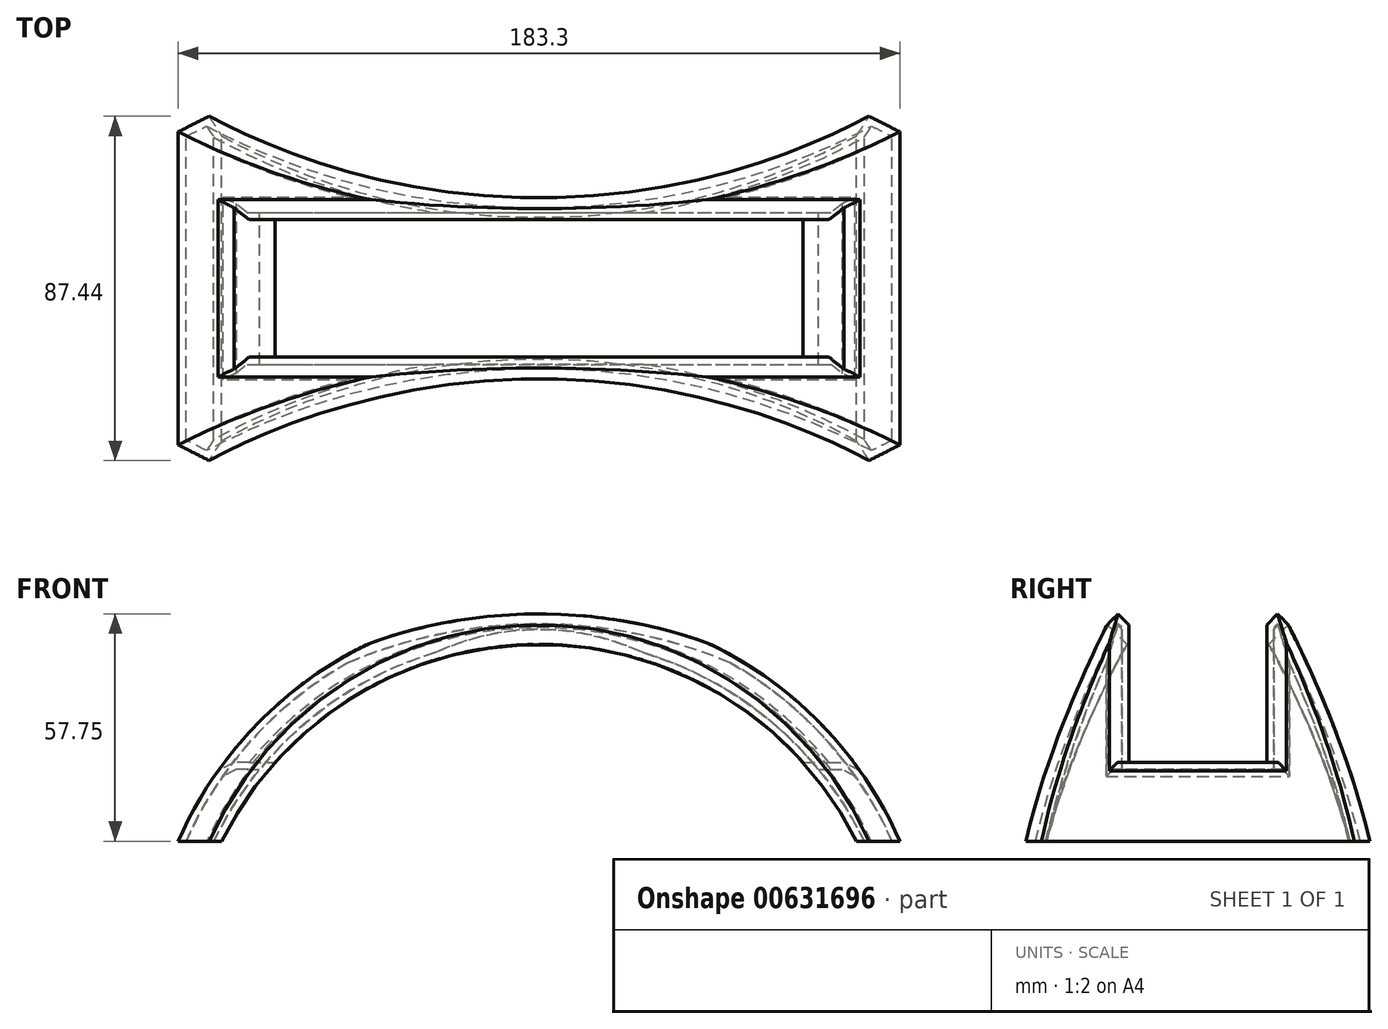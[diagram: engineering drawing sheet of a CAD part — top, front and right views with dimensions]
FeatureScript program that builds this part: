
annotation { "Feature Type Name" : "Feature", "Feature Type Description" : "" }
export const myFeature = defineFeature(function(context is Context, id is Id, definition is map)
    precondition{}
    {
        {
            var Q0;
            Q0=qCreatedBy(makeId("Front.planeOp"),FACE);
            var sketch = newSketch(context, id + "F0", { "sketchPlane" : qUnion([Q0])});
            skLineSegment(sketch, "E0", {"start": v(0, 0) * mm, "end": v(0, -40) * mm});
            skArc(sketch, "E1", {"start": v(91.65, 0) * mm, "mid": v(0, 60) * mm, "end": v(-91.65, 0) * mm});
            skArc(sketch, "E2", {"start": v(80.62, 0) * mm, "mid": v(0, 50) * mm, "end": v(-80.62, 0) * mm});
            skLineSegment(sketch, "E3", {"start": v(0, 0) * mm, "end": v(-91.65, 0) * mm});
            skLineSegment(sketch, "E4", {"start": v(0, 0) * mm, "end": v(91.65, 0) * mm});
            skLineSegment(sketch, "E5", {"start": v(0, 0) * mm, "end": v(0, 20) * mm});
            skSolve(sketch);
        }
        {
            var Q0;
            Q0=qCreatedBy(makeId("Top.planeOp"),FACE);
            cPlane(context, id + "F1", {"entities" : qUnion([Q0]), "cplaneType" : CPlaneType.OFFSET, "offset" : 20 * mm, "width" : 150 * mm, "height" : 150 * mm});
        }
        {
            var Q0;
            {var subQ0=sQuery(id+"F0.wireOp",EDGE,"E1");Q0=makeQuery(id+"F0.imprint","IMPRINT",FACE,{"disambiguationData":[TD([[makeQuery(id+"F0.imprint","IMPRINT",EDGE,{"derivedFrom":subQ0}),1.0]])]});}
            extrude(context, id + "F2", {"entities" : qUnion([Q0]), "depth" : 50 * mm, "offsetDistance" : 25 * mm, "hasSecondDirection" : true, "secondDirectionOppositeDirection" : true, "secondDirectionDepth" : 50 * mm});
        }
        {
            var Q0;
            Q0=qCreatedBy(id+"F1.planeOp",FACE);
            var sketch = newSketch(context, id + "F3", { "sketchPlane" : qUnion([Q0])});
            skLineSegment(sketch, "E6.bottom", {"start": v(-100, -17.5) * mm, "end": v(100, -17.5) * mm});
            skLineSegment(sketch, "E6.top", {"start": v(-100, 17.5) * mm, "end": v(100, 17.5) * mm});
            skLineSegment(sketch, "E6.left", {"start": v(-100, -17.5) * mm, "end": v(-100, 17.5) * mm});
            skLineSegment(sketch, "E6.right", {"start": v(100, -17.5) * mm, "end": v(100, 17.5) * mm});
            skPoint(sketch, "E6.middle", {"position": v(0, 0) * mm});
            skSolve(sketch);
        }
        {
            var Q0;
            Q0=makeQuery(id+"F3.imprint","IMPRINT",FACE,{"disambiguationData":[TD([[makeQuery(id+"F3.imprint","IMPRINT",EDGE,{"derivedFrom":sQuery(id+"F3.wireOp",EDGE,"E6.bottom")}),1.0]])]});
            extrude(context, id + "F4", {"entities" : qUnion([Q0]), "operationType" : NewBodyOperationType.REMOVE, "depth" : 50 * mm, "offsetDistance" : 25 * mm});
        }
        {
            var Q0;
            Q0=qCreatedBy(makeId("Top.planeOp"),FACE);
            var sketch = newSketch(context, id + "F5", { "sketchPlane" : qUnion([Q0])});
            skLineSegment(sketch, "E7", {"start": v(0, 0) * mm, "end": v(0, 23) * mm});
            skLineSegment(sketch, "E8", {"start": v(0, 0) * mm, "end": v(0, -23) * mm});
            skLineSegment(sketch, "E9", {"start": v(0, 23) * mm, "end": v(0, 203) * mm});
            skCircle(sketch, "E10", {"center": v(0, 203) * mm, "radius": 180 * mm});
            skLineSegment(sketch, "E11", {"start": v(0, -23) * mm, "end": v(0, -203) * mm});
            skCircle(sketch, "E12", {"center": v(0, -203) * mm, "radius": 180 * mm});
            skSolve(sketch);
        }
        {
            var Q0;
            Q0=makeQuery(id+"F5.imprint","IMPRINT",FACE,{"disambiguationData":[TD([[makeQuery(id+"F5.imprint","IMPRINT",EDGE,{"derivedFrom":sQuery(id+"F5.wireOp",EDGE,"E12")}),1.0]])]});
            var Q1;
            Q1=makeQuery(id+"F5.imprint","IMPRINT",FACE,{"disambiguationData":[TD([[makeQuery(id+"F5.imprint","IMPRINT",EDGE,{"derivedFrom":sQuery(id+"F5.wireOp",EDGE,"E10")}),1.0]])]});
            extrude(context, id + "F6", {"entities" : qUnion([Q0, Q1]), "operationType" : NewBodyOperationType.REMOVE, "depth" : 60 * mm, "offsetDistance" : 25 * mm});
        }
        {
            var Q0;
            Q0=makeQuery(id+"F6.boolean.opBoolean","INTERSECT",EDGE,{"derivedFrom":[makeQuery(id+"F2.opExtrude","SWEPT_FACE",FACE,{"disambiguationData":[OSD([sQuery(id+"F0.wireOp",EDGE,"E1")])]}),makeQuery(id+"F6.opExtrude","SWEPT_FACE",FACE,{"disambiguationData":[OSD([sQuery(id+"F5.wireOp",EDGE,"E12")])]})]});
            var Q1;
            Q1=makeQuery(id+"F6.boolean.opBoolean","INTERSECT",EDGE,{"derivedFrom":[makeQuery(id+"F2.opExtrude","SWEPT_FACE",FACE,{"disambiguationData":[OSD([sQuery(id+"F0.wireOp",EDGE,"E2")])]}),makeQuery(id+"F6.opExtrude","SWEPT_FACE",FACE,{"disambiguationData":[OSD([sQuery(id+"F5.wireOp",EDGE,"E12")])]})]});
            var Q2;
            Q2=makeQuery(id+"F6.boolean.opBoolean","INTERSECT",EDGE,{"derivedFrom":[makeQuery(id+"F2.opExtrude","SWEPT_FACE",FACE,{"disambiguationData":[OSD([sQuery(id+"F0.wireOp",EDGE,"E1")])]}),makeQuery(id+"F6.opExtrude","SWEPT_FACE",FACE,{"disambiguationData":[OSD([sQuery(id+"F5.wireOp",EDGE,"E10")])]})]});
            var Q3;
            Q3=makeQuery(id+"F6.boolean.opBoolean","INTERSECT",EDGE,{"derivedFrom":[makeQuery(id+"F2.opExtrude","SWEPT_FACE",FACE,{"disambiguationData":[OSD([sQuery(id+"F0.wireOp",EDGE,"E2")])]}),makeQuery(id+"F6.opExtrude","SWEPT_FACE",FACE,{"disambiguationData":[OSD([sQuery(id+"F5.wireOp",EDGE,"E10")])]})]});
            var Q4;
            Q4=makeQuery(id+"F4.boolean.opBoolean","INTERSECT",EDGE,{"derivedFrom":[makeQuery(id+"F2.opExtrude","SWEPT_FACE",FACE,{"disambiguationData":[OSD([sQuery(id+"F0.wireOp",EDGE,"E1")])]}),makeQuery(id+"F4.opExtrude","SWEPT_FACE",FACE,{"disambiguationData":[OSD([sQuery(id+"F3.wireOp",EDGE,"E6.top")])]})]});
            var Q5;
            Q5=makeQuery(id+"F4.boolean.opBoolean","INTERSECT",EDGE,{"derivedFrom":[makeQuery(id+"F2.opExtrude","SWEPT_FACE",FACE,{"disambiguationData":[OSD([sQuery(id+"F0.wireOp",EDGE,"E1")])]}),makeQuery(id+"F4.opExtrude","SWEPT_FACE",FACE,{"disambiguationData":[OSD([sQuery(id+"F3.wireOp",EDGE,"E6.bottom")])]})]});
            chamfer(context, id + "F7", {"entities" : qUnion([Q0, Q1, Q2, Q3, Q4, Q5]), "width" : 5 * mm, "tangentPropagation" : true});
        }
        {
            var Q0;
            Q0=makeQuery(id+"F4.boolean.opBoolean","INTERSECT",EDGE,{"disambiguationData":[OD(0.0)],"derivedFrom":[makeQuery(id+"F2.opExtrude","SWEPT_FACE",FACE,{"disambiguationData":[OSD([sQuery(id+"F0.wireOp",EDGE,"E1")])]}),makeQuery(id+"F4.opExtrude","CAP_FACE",FACE,{"disambiguationData":[OSD([sQuery(id+"F3.wireOp",EDGE,"E6.bottom"),sQuery(id+"F3.wireOp",EDGE,"E6.top"),sQuery(id+"F3.wireOp",EDGE,"E6.left"),sQuery(id+"F3.wireOp",EDGE,"E6.right")])],"isStart":true})]});
            var Q1;
            Q1=makeQuery(id+"F4.boolean.opBoolean","INTERSECT",EDGE,{"disambiguationData":[OD(1.0)],"derivedFrom":[makeQuery(id+"F2.opExtrude","SWEPT_FACE",FACE,{"disambiguationData":[OSD([sQuery(id+"F0.wireOp",EDGE,"E1")])]}),makeQuery(id+"F4.opExtrude","CAP_FACE",FACE,{"disambiguationData":[OSD([sQuery(id+"F3.wireOp",EDGE,"E6.bottom"),sQuery(id+"F3.wireOp",EDGE,"E6.top"),sQuery(id+"F3.wireOp",EDGE,"E6.left"),sQuery(id+"F3.wireOp",EDGE,"E6.right")])],"isStart":true})]});
            chamfer(context, id + "F8", {"entities" : qUnion([Q0, Q1]), "width" : 5 * mm, "tangentPropagation" : true});
        }
        {
            var Q0;
            Q0=makeQuery(id+"F2.opExtrude","SWEPT_FACE",FACE,{"disambiguationData":[OSD([sQuery(id+"F0.wireOp",EDGE,"E4")])]});
            var Q1;
            Q1=makeQuery(id+"F2.opExtrude","SWEPT_FACE",FACE,{"disambiguationData":[OSD([sQuery(id+"F0.wireOp",EDGE,"E3")])]});
            shell(context, id + "F9", {"entities" : qUnion([Q0, Q1]), "thickness" : 1.8 * mm});
        }
    });
